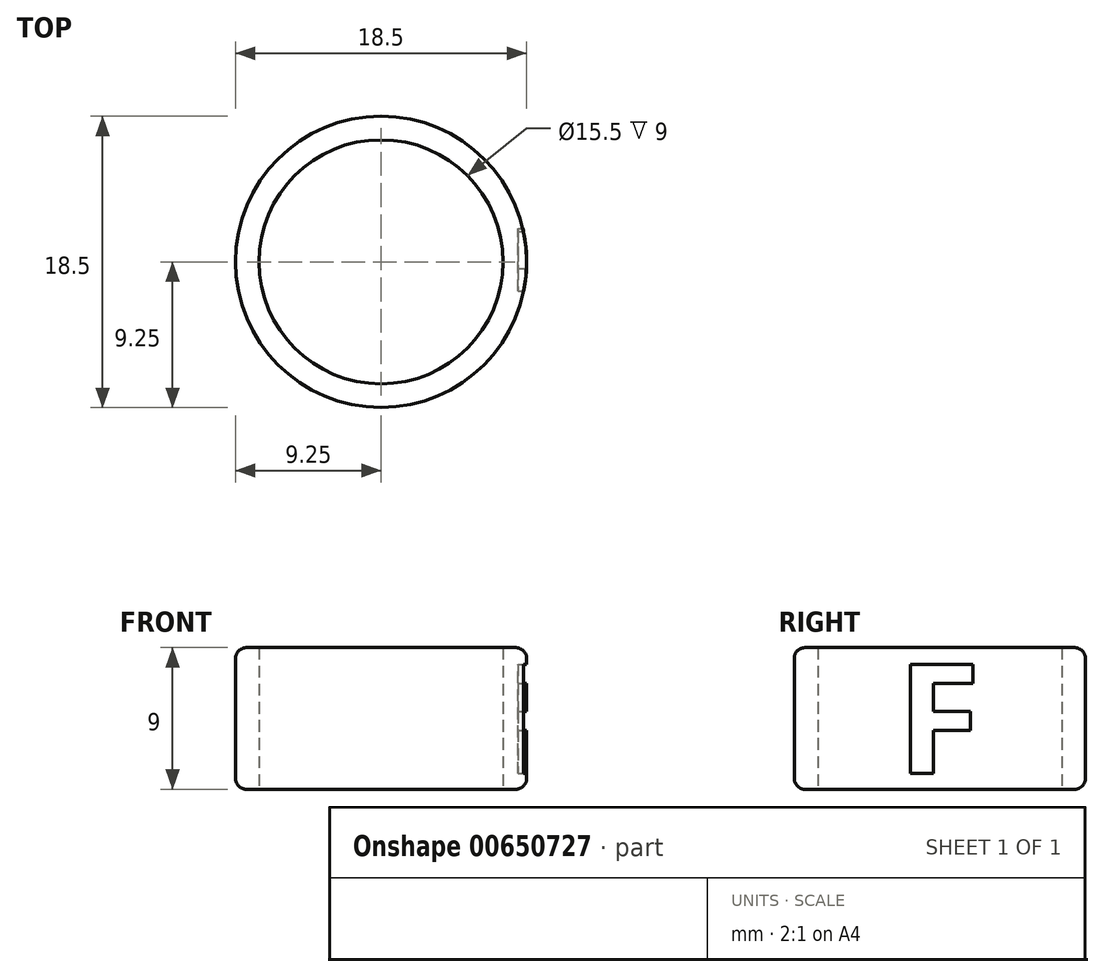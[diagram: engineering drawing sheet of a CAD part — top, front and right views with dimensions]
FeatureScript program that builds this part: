
annotation { "Feature Type Name" : "Feature", "Feature Type Description" : "" }
export const myFeature = defineFeature(function(context is Context, id is Id, definition is map)
    precondition{}
    {
        {
            var Q0;
            Q0=qCreatedBy(makeId("Top.planeOp"),FACE);
            var sketch = newSketch(context, id + "F0", { "sketchPlane" : qUnion([Q0])});
            skCircle(sketch, "E0", {"center": v(0, 0) * mm, "radius": 7.75 * mm});
            skCircle(sketch, "E1", {"center": v(0, 0) * mm, "radius": 9.25 * mm});
            skSolve(sketch);
        }
        {
            var Q0;
            Q0=makeQuery(id+"F0.imprint","IMPRINT",FACE,{"disambiguationData":[TD([[makeQuery(id+"F0.imprint","IMPRINT",EDGE,{"derivedFrom":sQuery(id+"F0.wireOp",EDGE,"E0")}),-1.0]])]});
            extrude(context, id + "F1", {"entities" : qUnion([Q0]), "depth" : 4.5 * mm, "offsetDistance" : 25 * mm, "hasSecondDirection" : true, "secondDirectionOppositeDirection" : true, "secondDirectionDepth" : 4.5 * mm});
        }
        {
            var Q0;
            Q0=makeQuery(id+"F1.opExtrude","CAP_EDGE",EDGE,{"disambiguationData":[OSD([sQuery(id+"F0.wireOp",EDGE,"E1")])],"isStart":false});
            var Q1;
            Q1=makeQuery(id+"F1.opExtrude","CAP_EDGE",EDGE,{"disambiguationData":[OSD([sQuery(id+"F0.wireOp",EDGE,"E1")])],"isStart":true});
            fillet(context, id + "F2", {"entities" : qUnion([Q0, Q1]), "radius" : 0.7 * mm, "tangentPropagation" : true, "allowEdgeOverflow" : false});
        }
        {
            var Q0;
            Q0=qCreatedBy(makeId("Right.planeOp"),FACE);
            cPlane(context, id + "F3", {"entities" : qUnion([Q0]), "cplaneType" : CPlaneType.OFFSET, "offset" : 10 * mm, "width" : 150 * mm, "height" : 150 * mm});
        }
        {
            var Q0;
            Q0=qCreatedBy(id+"F3.planeOp",FACE);
            var sketch = newSketch(context, id + "F4", { "sketchPlane" : qUnion([Q0])});
            skText(sketch, "E2", { "text": "F", "fontName": "OpenSans-Bold.ttf"});
            skLineSegment(sketch, "E3", {"start": v(0, 0.65) * mm, "end": v(3.37, 0.65) * mm, "construction": true});
            skLineSegment(sketch, "E4", {"start": v(0, 0.65) * mm, "end": v(0, -3.5) * mm, "construction": true});
            const initialGuessF4  = {"E2": [-0.00274, -0.0035, 1, 0, 0.007]};
            skSetInitialGuess(sketch, initialGuessF4);
            skSolve(sketch);
        }
        {
            var Q0;
            Q0=makeQuery(id+"F4.imprint","IMPRINT",FACE,{"disambiguationData":[TD([[makeQuery(id+"F4.imprint","IMPRINT",EDGE,{"derivedFrom":sQuery(id+"F4.wireOp",EDGE,"E2.sketch_text.stroke-0")}),-1.0]])]});
            extrude(context, id + "F5", {"entities" : qUnion([Q0]), "operationType" : NewBodyOperationType.REMOVE, "oppositeDirection" : true, "depth" : 1.3 * mm, "offsetDistance" : 25 * mm});
        }
    });
